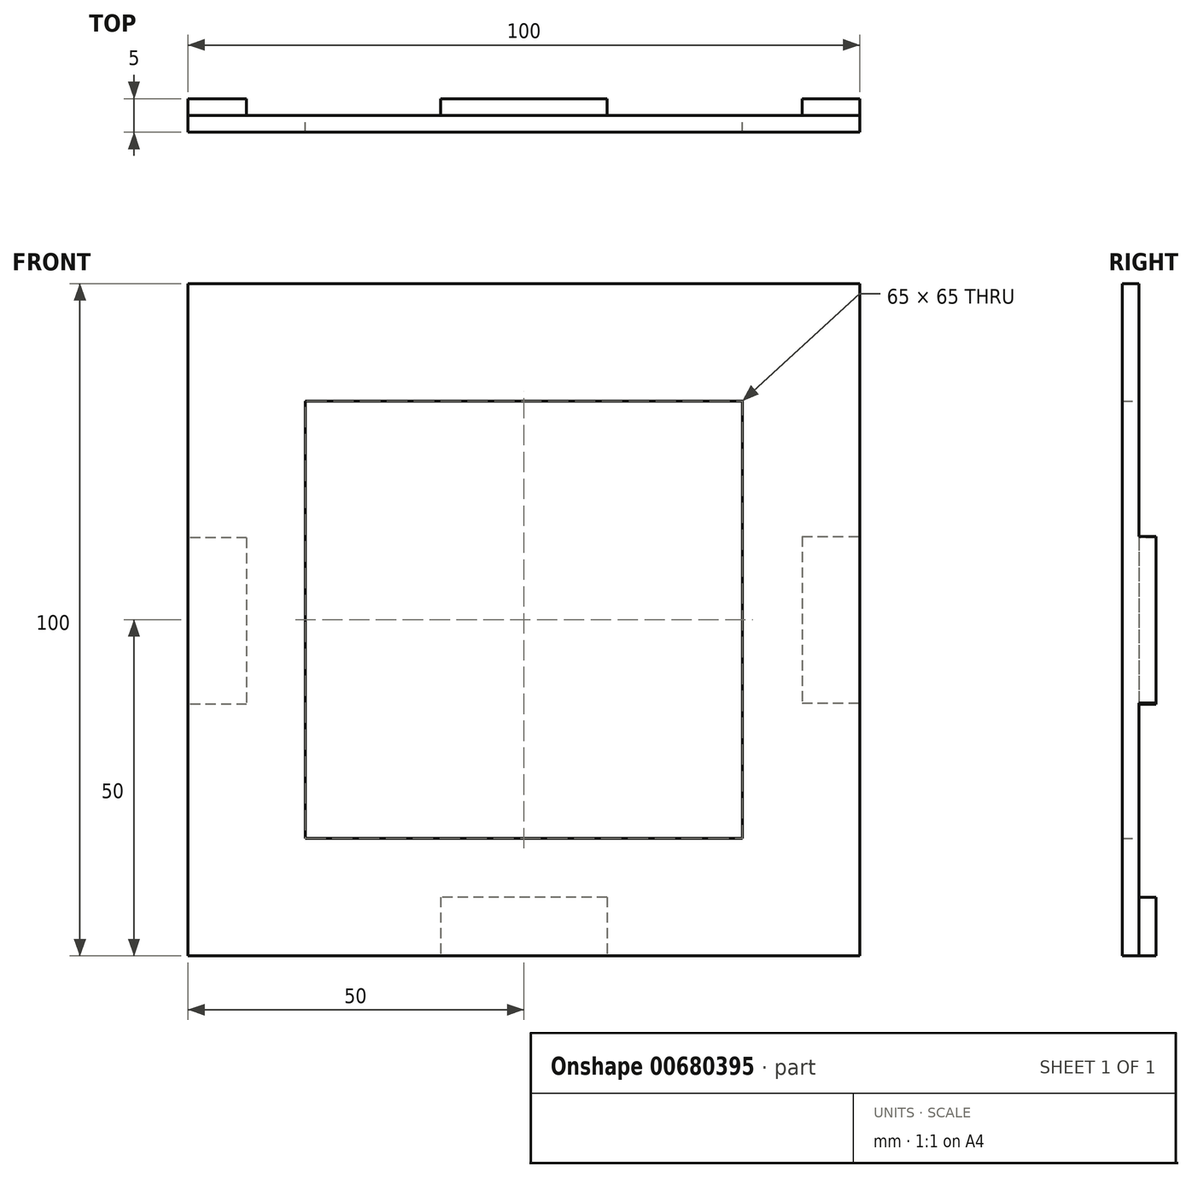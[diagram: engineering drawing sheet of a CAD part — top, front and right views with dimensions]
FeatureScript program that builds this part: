
annotation { "Feature Type Name" : "Feature", "Feature Type Description" : "" }
export const myFeature = defineFeature(function(context is Context, id is Id, definition is map)
    precondition{}
    {
        {
            var Q0;
            Q0=qCreatedBy(makeId("Front.planeOp"),FACE);
            var sketch = newSketch(context, id + "F0", { "sketchPlane" : qUnion([Q0])});
            skLineSegment(sketch, "E0.bottom", {"start": v(50, 50) * mm, "end": v(-50, 50) * mm});
            skLineSegment(sketch, "E0.top", {"start": v(50, -50) * mm, "end": v(-50, -50) * mm});
            skLineSegment(sketch, "E0.left", {"start": v(50, 50) * mm, "end": v(50, -50) * mm});
            skLineSegment(sketch, "E0.right", {"start": v(-50, 50) * mm, "end": v(-50, -50) * mm});
            skPoint(sketch, "E0.middle", {"position": v(0, 0) * mm});
            skLineSegment(sketch, "E1.bottom", {"start": v(32.5, 32.5) * mm, "end": v(-32.5, 32.5) * mm});
            skLineSegment(sketch, "E1.top", {"start": v(32.5, -32.5) * mm, "end": v(-32.5, -32.5) * mm});
            skLineSegment(sketch, "E1.left", {"start": v(32.5, 32.5) * mm, "end": v(32.5, -32.5) * mm});
            skLineSegment(sketch, "E1.right", {"start": v(-32.5, 32.5) * mm, "end": v(-32.5, -32.5) * mm});
            skSolve(sketch);
        }
        {
            var Q0;
            Q0 = qSketchRegion(id + "F0", true);
            extrude(context, id + "F1", {"entities" : qUnion([Q0]), "depth" : 2.5 * mm, "offsetDistance" : 25 * mm});
        }
        {
            var Q0;
            Q0=makeQuery(id+"F1.opExtrude","CAP_FACE",FACE,{"disambiguationData":[OSD([sQuery(id+"F0.wireOp",EDGE,"E0.bottom"),sQuery(id+"F0.wireOp",EDGE,"E0.top"),sQuery(id+"F0.wireOp",EDGE,"E0.left"),sQuery(id+"F0.wireOp",EDGE,"E0.right"),sQuery(id+"F0.wireOp",EDGE,"E1.bottom"),sQuery(id+"F0.wireOp",EDGE,"E1.top"),sQuery(id+"F0.wireOp",EDGE,"E1.left"),sQuery(id+"F0.wireOp",EDGE,"E1.right")])],"isStart":true});
            var sketch = newSketch(context, id + "F2", { "sketchPlane" : qUnion([Q0])});
            skLineSegment(sketch, "E2.left", {"start": v(41.25, 12.18) * mm, "end": v(41.25, -12.56) * mm});
            skPoint(sketch, "E2.middle", {"position": v(50, 0) * mm});
            skLineSegment(sketch, "E3", {"start": v(41.25, 12.18) * mm, "end": v(50, 12.18) * mm});
            skLineSegment(sketch, "E4", {"start": v(41.25, -12.56) * mm, "end": v(50, -12.56) * mm});
            skSolve(sketch);
        }
        {
            var Q0;
            Q0=makeQuery(id+"F2.imprint","IMPRINT",FACE,{"disambiguationData":[TD([[makeQuery(id+"F2.imprint","IMPRINT",EDGE,{"derivedFrom":sQuery(id+"F2.wireOp",EDGE,"E2.left")}),1.0]])]});
            extrude(context, id + "F3", {"entities" : qUnion([Q0]), "operationType" : NewBodyOperationType.ADD, "depth" : 2.5 * mm, "offsetDistance" : 25 * mm});
        }
        {
            var Q0;
            Q0=makeQuery(id+"F2.imprint","IMPRINT",FACE,{"disambiguationData":[TD([[makeQuery(id+"F2.imprint","IMPRINT",EDGE,{"derivedFrom":sQuery(id+"F2.wireOp",EDGE,"E2.left")}),-1.0]])]});
            var sketch = newSketch(context, id + "F4", { "sketchPlane" : qUnion([Q0])});
            skLineSegment(sketch, "E5.left", {"start": v(-41.39, 12.37) * mm, "end": v(-41.39, -12.37) * mm});
            skPoint(sketch, "E5.middle", {"position": v(-50.53, 0) * mm});
            skLineSegment(sketch, "E6", {"start": v(-41.39, 12.37) * mm, "end": v(-50.14, 12.37) * mm});
            skLineSegment(sketch, "E7", {"start": v(-41.39, -12.37) * mm, "end": v(-50.78, -12.37) * mm});
            skSolve(sketch);
        }
        {
            var Q0;
            {var subQ0=sQuery(id+"F4.wireOp",EDGE,"E5.left");Q0=makeQuery(id+"F4.imprint","IMPRINT",FACE,{"disambiguationData":[TD([[makeQuery(id+"F4.imprint","IMPRINT",EDGE,{"derivedFrom":subQ0}),-1.0]])]});}
            extrude(context, id + "F5", {"entities" : qUnion([Q0]), "operationType" : NewBodyOperationType.ADD, "depth" : 2.5 * mm, "offsetDistance" : 25 * mm});
        }
        {
            var Q0;
            Q0=makeQuery(id+"F1.opExtrude","SWEPT_FACE",FACE,{"disambiguationData":[OSD([sQuery(id+"F0.wireOp",EDGE,"E0.top")])]});
            var sketch = newSketch(context, id + "F6", { "sketchPlane" : qUnion([Q0])});
            skPoint(sketch, "E8.middle", {"position": v(0, 58.75) * mm});
            skLineSegment(sketch, "E9.bottom", {"start": v(-12.37, -2.5) * mm, "end": v(12.37, -2.5) * mm});
            skPoint(sketch, "E9.middle", {"position": v(0, 0) * mm});
            skLineSegment(sketch, "E10", {"start": v(-12.37, -2.5) * mm, "end": v(-12.37, 0) * mm});
            skLineSegment(sketch, "E11", {"start": v(12.37, -2.5) * mm, "end": v(12.37, 0) * mm});
            skSolve(sketch);
        }
        {
            var Q0;
            Q0=makeQuery(id+"F6.imprint","IMPRINT",FACE,{"disambiguationData":[TD([[makeQuery(id+"F6.imprint","IMPRINT",EDGE,{"derivedFrom":sQuery(id+"F6.wireOp",EDGE,"E9.bottom")}),1.0]])]});
            extrude(context, id + "F7", {"entities" : qUnion([Q0]), "operationType" : NewBodyOperationType.ADD, "oppositeDirection" : true, "depth" : 8.75 * mm, "offsetDistance" : 25 * mm});
        }
    });
